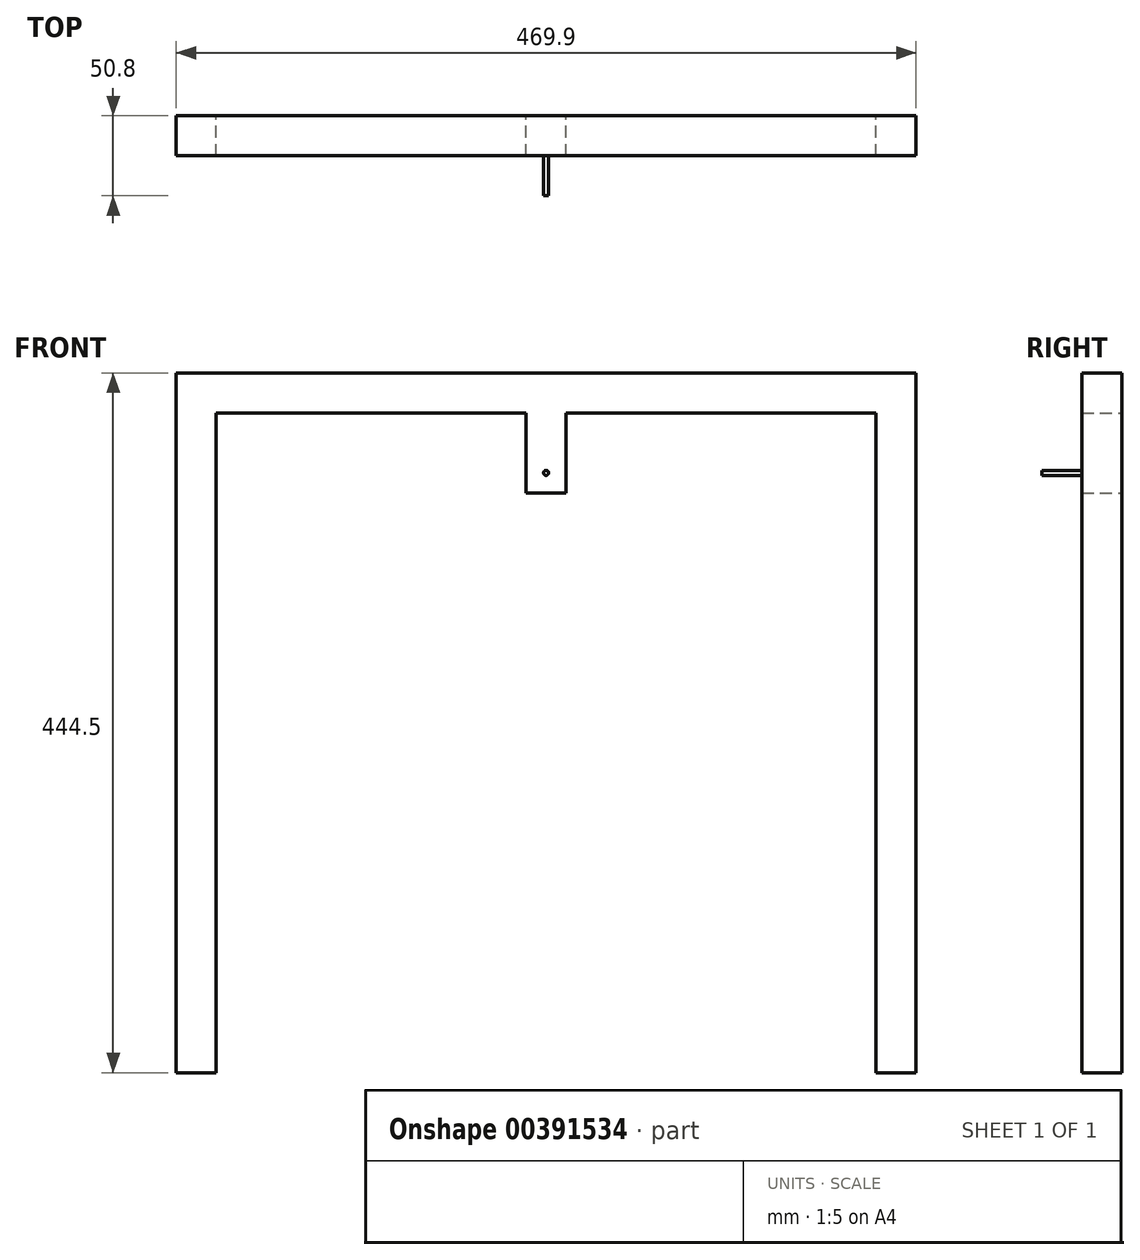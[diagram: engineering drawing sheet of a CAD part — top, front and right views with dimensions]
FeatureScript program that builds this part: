
annotation { "Feature Type Name" : "Feature", "Feature Type Description" : "" }
export const myFeature = defineFeature(function(context is Context, id is Id, definition is map)
    precondition{}
    {
        {
            var Q0;
            Q0=qCreatedBy(makeId("Top.planeOp"),FACE);
            var sketch = newSketch(context, id + "F0", { "sketchPlane" : qUnion([Q0])});
            skLineSegment(sketch, "E0.bottom", {"start": v(-209.55, 12.7) * mm, "end": v(-234.95, 12.7) * mm});
            skLineSegment(sketch, "E0.top", {"start": v(-209.55, -12.7) * mm, "end": v(-234.95, -12.7) * mm});
            skLineSegment(sketch, "E0.left", {"start": v(-209.55, 12.7) * mm, "end": v(-209.55, -12.7) * mm});
            skLineSegment(sketch, "E0.right", {"start": v(-234.95, 12.7) * mm, "end": v(-234.95, -12.7) * mm});
            skPoint(sketch, "E0.middle", {"position": v(-222.25, 0) * mm});
            skSolve(sketch);
        }
        {
            var Q0;
            Q0=makeQuery(id+"F0.imprint","IMPRINT",FACE,{"disambiguationData":[TD([[makeQuery(id+"F0.imprint","IMPRINT",EDGE,{"derivedFrom":sQuery(id+"F0.wireOp",EDGE,"E0.bottom")}),1.0]])]});
            extrude(context, id + "F1", {"entities" : qUnion([Q0]), "depth" : 444.5 * mm, "offsetDistance" : 25.4 * mm});
        }
        {
            var Q0;
            Q0=makeQuery(id+"F1.opExtrude","SWEPT_FACE",FACE,{"disambiguationData":[OSD([sQuery(id+"F0.wireOp",EDGE,"E0.left")])]});
            var sketch = newSketch(context, id + "F2", { "sketchPlane" : qUnion([Q0])});
            skLineSegment(sketch, "E1.bottom", {"start": v(-12.7, 444.5) * mm, "end": v(12.7, 444.5) * mm});
            skLineSegment(sketch, "E1.top", {"start": v(-12.7, 419.1) * mm, "end": v(12.7, 419.1) * mm});
            skLineSegment(sketch, "E1.left", {"start": v(-12.7, 444.5) * mm, "end": v(-12.7, 419.1) * mm});
            skLineSegment(sketch, "E1.right", {"start": v(12.7, 444.5) * mm, "end": v(12.7, 419.1) * mm});
            skSolve(sketch);
        }
        {
            var Q0;
            Q0=makeQuery(id+"F2.imprint","IMPRINT",FACE,{"disambiguationData":[TD([[makeQuery(id+"F2.imprint","IMPRINT",EDGE,{"derivedFrom":sQuery(id+"F2.wireOp",EDGE,"E1.bottom")}),1.0]])]});
            extrude(context, id + "F3", {"entities" : qUnion([Q0]), "operationType" : NewBodyOperationType.ADD, "depth" : 209.55 * mm, "offsetDistance" : 25.4 * mm});
        }
        {
            var Q0;
            Q0=makeQuery(id+"F1.opExtrude","SWEPT_BODY",BODY,{"disambiguationData":[OSD([sQuery(id+"F0.wireOp",EDGE,"E0.bottom"),sQuery(id+"F0.wireOp",EDGE,"E0.top"),sQuery(id+"F0.wireOp",EDGE,"E0.left"),sQuery(id+"F0.wireOp",EDGE,"E0.right")])]});
            var Q1;
            Q1=qCreatedBy(makeId("Right.planeOp"),FACE);
            mirror(context, id + "F4", {"operationType" : NewBodyOperationType.ADD, "entities" : qUnion([Q0]), "mirrorPlane" : qUnion([Q1])});
        }
        {
            var Q0;
            {var subQ0=makeQuery(id+"F3.opExtrude","SWEPT_FACE",FACE,{"disambiguationData":[OSD([sQuery(id+"F2.wireOp",EDGE,"E1.top")])]});Q0=makeQuery(id+"F4.boolean.opBoolean","MERGE",FACE,{"derivedFrom":[subQ0,makeQuery(id+"F4.opPattern","COPY",FACE,{"derivedFrom":subQ0,"instanceName":"1"})]});}
            var sketch = newSketch(context, id + "F5", { "sketchPlane" : qUnion([Q0])});
            skLineSegment(sketch, "E2.bottom", {"start": v(12.7, 12.7) * mm, "end": v(-12.7, 12.7) * mm});
            skLineSegment(sketch, "E2.top", {"start": v(12.7, -12.7) * mm, "end": v(-12.7, -12.7) * mm});
            skLineSegment(sketch, "E2.left", {"start": v(12.7, 12.7) * mm, "end": v(12.7, -12.7) * mm});
            skLineSegment(sketch, "E2.right", {"start": v(-12.7, 12.7) * mm, "end": v(-12.7, -12.7) * mm});
            skPoint(sketch, "E2.middle", {"position": v(0, 0) * mm});
            skSolve(sketch);
        }
        {
            var Q0;
            Q0 = qSketchRegion(id + "F5", true);
            extrude(context, id + "F6", {"entities" : qUnion([Q0]), "operationType" : NewBodyOperationType.ADD, "depth" : 50.8 * mm, "offsetDistance" : 25.4 * mm});
        }
        {
            var Q0;
            {var subQ0=makeQuery(id+"F3.boolean.opBoolean","MERGE",FACE,{"derivedFrom":[makeQuery(id+"F1.opExtrude","SWEPT_FACE",FACE,{"disambiguationData":[OSD([sQuery(id+"F0.wireOp",EDGE,"E0.top")])]}),makeQuery(id+"F3.opExtrude","SWEPT_FACE",FACE,{"disambiguationData":[OSD([sQuery(id+"F2.wireOp",EDGE,"E1.left")])]})]});Q0=makeQuery(id+"F6.boolean.opBoolean","MERGE",FACE,{"derivedFrom":[makeQuery(id+"F4.boolean.opBoolean","MERGE",FACE,{"derivedFrom":[subQ0,makeQuery(id+"F4.opPattern","COPY",FACE,{"derivedFrom":subQ0,"instanceName":"1"})]}),makeQuery(id+"F6.opExtrude","SWEPT_FACE",FACE,{"disambiguationData":[OSD([sQuery(id+"F5.wireOp",EDGE,"E2.bottom")])]})]});}
            var sketch = newSketch(context, id + "F7", { "sketchPlane" : qUnion([Q0])});
            skCircle(sketch, "E3", {"center": v(0, 381) * mm, "radius": 1.59 * mm});
            skSolve(sketch);
        }
        {
            var Q0;
            Q0 = qSketchRegion(id + "F7", true);
            extrude(context, id + "F8", {"entities" : qUnion([Q0]), "operationType" : NewBodyOperationType.ADD, "depth" : 25.4 * mm, "offsetDistance" : 25.4 * mm});
        }
    });
